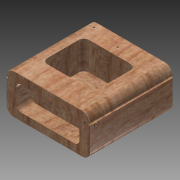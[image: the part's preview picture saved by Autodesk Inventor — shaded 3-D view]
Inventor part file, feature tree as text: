
AUTODESK INVENTOR PART (.ipt)
format: ipt  version: 2015 (Build 190159000, 159)  size: 349,696 bytes
history: native  units: in
note: dims shown in document units (in); Inventor stores cm internally (conversion verified against a paired STEP export)
features: sketch x7, extrude x6, chamfer x4, emboss x1
ambient origin geometry x8: Origin, YZ Plane, XZ Plane, XY Plane, X Axis, Y Axis, Z Axis, Center Point
bodies: Solid1 (feature_tree)
feature tree (18):
  extrude  "Extrusion1"  Depth=3.17in
  extrude  "Extrusion2"  Depth=3.17in TaperAngle=0.0deg
  extrude  "Extrusion3"  Depth=1.59in
  extrude  "Extrusion4"  Depth=0.2in TaperAngle=0.0deg
  extrude  "Extrusion5"  Depth=2.4in
  extrude  "Extrusion6"  Depth=0.3in
  emboss  "Emboss1"
  chamfer  "Chamfer1"  Distance=0.57in
  chamfer  "Chamfer2"  Distance=2.5in
  chamfer  "Chamfer3"  Distance=1.0in
  chamfer  "Chamfer4"  Distance=0.34in
  sketch  "Sketch1"  dims[d0=1.53in d1=3.17in]
  sketch  "Sketch2"  dims[d2=0.3in d3=3.17in d4=0.0in]
  sketch  "Sketch3"  dims[d7=1.98in d8=1.59in]
  sketch  "Sketch4"  dims[d10=0.2in d11=1.07in d12=0.0in]
  sketch  "Sketch5"  dims[d17=0.93in d18=2.4in]
  sketch  "Sketch6"  dims[d19=0.38in d20=0.3in]
  sketch  "Sketch7"  dims[d21=0.2in d22=0.57in d23=0.0in d24=2.5in d25=1.0in d26=0.34in d27=0.26in d28=0.2in d29=0.57in d30=0.0in d31=0.06in d32=3.17in d33=0.06in d34=0.0in d35=0.06in d36=3.17in d37=0.06in d38=0.0in d39=0.02in d40=0.0in d41=0.015in d42=0.125in d43=45.0deg d44=0.015in d45=0.125in d46=45.0deg d47=0.015in d48=0.125in d49=45.0deg d50=0.015in d51=0.125in d52=45.0deg]
